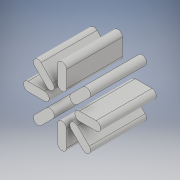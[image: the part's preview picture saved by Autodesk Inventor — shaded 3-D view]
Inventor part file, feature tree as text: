
AUTODESK INVENTOR PART (.ipt)
format: ipt  version: 2019 (Build 230136000, 136)  size: 157,184 bytes
history: native  units: mm
features: extrude x1, sketch x1
ambient origin geometry x8: Origin, YZ Plane, XZ Plane, XY Plane, X Axis, Y Axis, Z Axis, Center Point
bodies: Solid1 (feature_tree)
feature tree (2):
  extrude  "Extrusion1"  Depth=50.0mm
  sketch  "Sketch1"  dims[d0=4.0mm d1=15.0mm d2=80.0mm d4=360.0deg d6=50.0mm d7=0.0mm]
